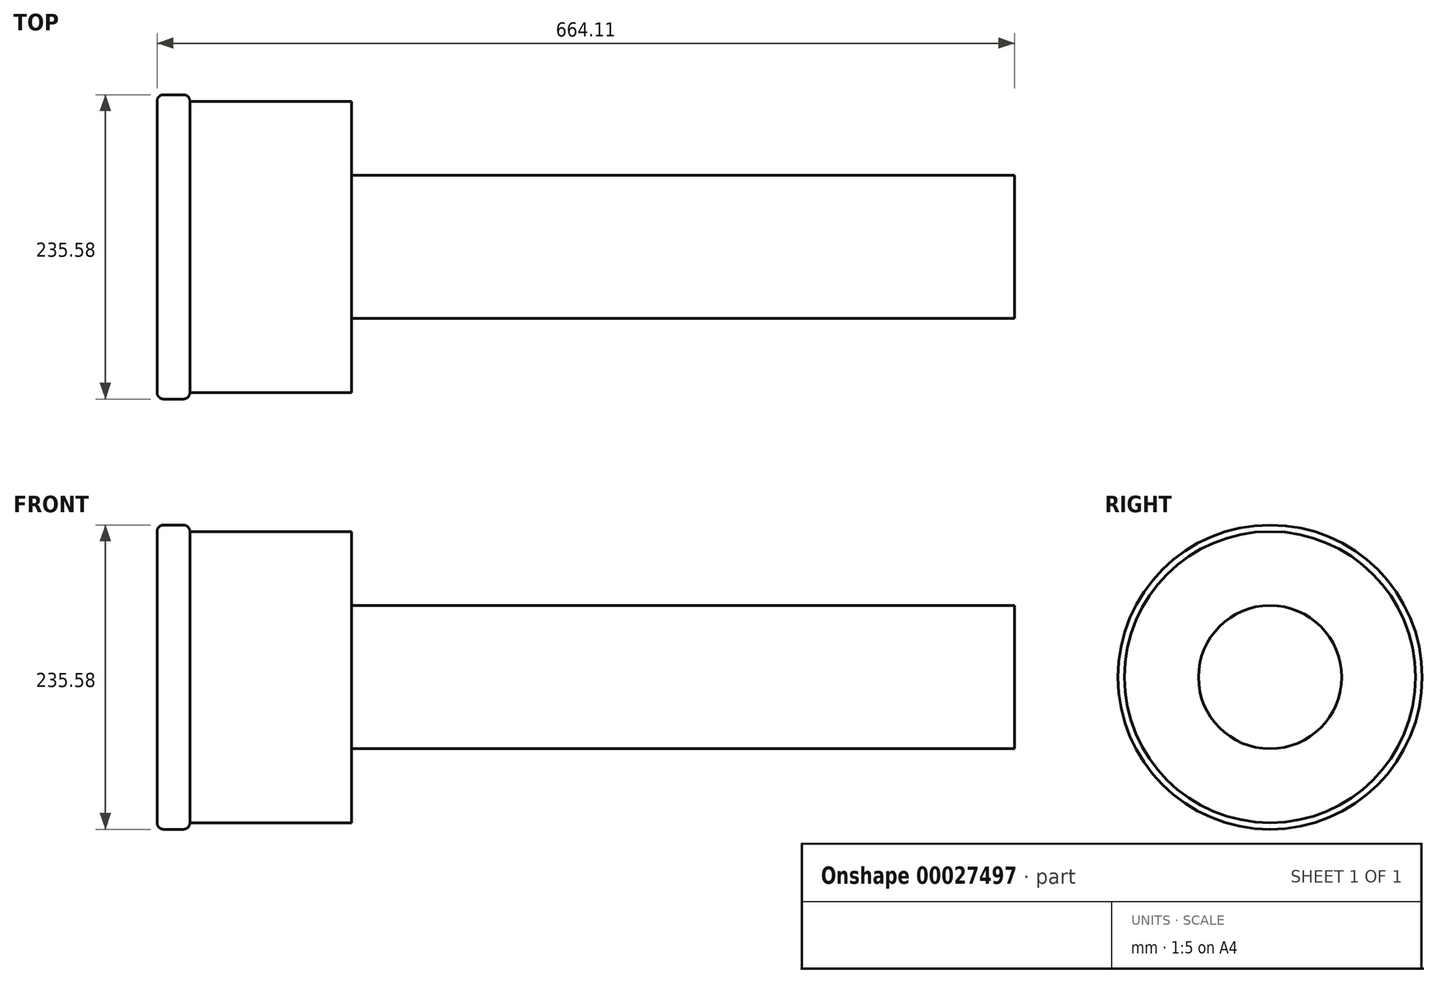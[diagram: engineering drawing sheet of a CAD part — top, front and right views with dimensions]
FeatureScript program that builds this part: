
annotation { "Feature Type Name" : "Feature", "Feature Type Description" : "" }
export const myFeature = defineFeature(function(context is Context, id is Id, definition is map)
    precondition{}
    {
        {
            var Q0;
            Q0=qCreatedBy(makeId("Right.planeOp"),FACE);
            var sketch = newSketch(context, id + "F0", { "sketchPlane" : qUnion([Q0])});
            skCircle(sketch, "E0", {"center": v(-7.24, -54.91) * mm, "radius": 117.8 * mm});
            skCircle(sketch, "E1", {"center": v(0, 0) * mm, "radius": 117.8 * mm});
            skSolve(sketch);
        }
        {
            var Q0;
            Q0=makeQuery(id+"F0.imprint","IMPRINT",FACE,{"disambiguationData":[TD([[makeQuery(id+"F0.imprint","IMPRINT",EDGE,{"derivedFrom":sQuery(id+"F0.wireOp",EDGE,"E0")}),1.0]])]});
            extrude(context, id + "F1", {"entities" : qUnion([Q0]), "depth" : 25.4 * mm});
        }
        {
            var Q0;
            Q0=makeQuery(id+"F1.opExtrude","CAP_EDGE",EDGE,{"disambiguationData":[OSD([sQuery(id+"F0.wireOp",EDGE,"E0")])],"isStart":true});
            var Q1;
            Q1=makeQuery(id+"F1.opExtrude","CAP_EDGE",EDGE,{"disambiguationData":[OSD([sQuery(id+"F0.wireOp",EDGE,"E0")])],"isStart":false});
            fillet(context, id + "F2", {"entities" : qUnion([Q0, Q1]), "radius" : 5.08 * mm, "tangentPropagation" : true, "allowEdgeOverflow" : false});
        }
        {
            var Q0;
            Q0=makeQuery(id+"F1.opExtrude","CAP_FACE",FACE,{"disambiguationData":[OSD([sQuery(id+"F0.wireOp",EDGE,"E0")])],"isStart":false});
            var sketch = newSketch(context, id + "F3", { "sketchPlane" : qUnion([Q0])});
            skSolve(sketch);
        }
        {
            var Q0;
            {var subQ0=sQuery(id+"F0.wireOp",EDGE,"E0");Q0=makeQuery(id+"F3.imprint","IMPRINT",FACE,{"disambiguationData":[TD([[makeQuery(id+"F3.imprint","IMPRINT",EDGE,{"derivedFrom":makeQuery(id+"F2.opFillet","BLEND_EDGE",EDGE,{"blendedFrom":[makeQuery(id+"F1.opExtrude","CAP_EDGE",EDGE,{"disambiguationData":[OSD([subQ0])],"isStart":false}),makeQuery(id+"F1.opExtrude","CAP_FACE",FACE,{"disambiguationData":[OSD([subQ0])],"isStart":false})],"blendedInto":[makeQuery(id+"F1.opExtrude","CAP_FACE",FACE,{"disambiguationData":[OSD([subQ0])],"isStart":false})]})}),1.0]])]});}
            extrude(context, id + "F4", {"entities" : qUnion([Q0]), "operationType" : NewBodyOperationType.ADD, "depth" : 125.22 * mm});
        }
        {
            var Q0;
            Q0=makeQuery(id+"F4.opExtrude","CAP_FACE",FACE,{"disambiguationData":[OSD([sQuery(id+"F0.wireOp",EDGE,"E0")])],"isStart":false});
            var sketch = newSketch(context, id + "F5", { "sketchPlane" : qUnion([Q0])});
            skCircle(sketch, "E2", {"center": v(-7.24, -54.91) * mm, "radius": 55.45 * mm});
            skSolve(sketch);
        }
        {
            var Q0;
            Q0 = qSketchRegion(id + "F5", true);
            extrude(context, id + "F6", {"entities" : qUnion([Q0]), "operationType" : NewBodyOperationType.ADD, "depth" : 513.5 * mm});
        }
    });
